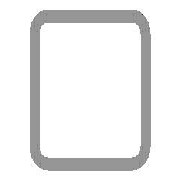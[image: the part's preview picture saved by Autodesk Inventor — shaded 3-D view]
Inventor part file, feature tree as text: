
AUTODESK INVENTOR PART (.ipt)
format: ipt  version: 2025.1 (Build 291241020, 241B)  size: 133,120 bytes
history: native  units: mm (DEFAULTED — no unit token found)
features: other x4, sketch x1, plane x1
ambient origin geometry x8: Origin, YZ Plane, XZ Plane, XY Plane, X Axis, Y Axis, Z Axis, Center Point
bodies: Solid1 (feature_tree), Body (feature_tree)
feature tree (6):
  parser-record x1  (decoder bookkeeping rows leaked as tree rows — omitted from the tree; the rows remain in map.json)
  other  "Driven Length"
  other  "Start Plane"
  other  "End Plane"
  sketch  "Sketch3"  dims[d3=1600.0mm d4=0.0mm d7=4.0mm d9=40.0mm d11=40.0mm d12=2.0mm d13=-0.0mm d14=1600.0mm d15=20.0mm d16=20.0mm d17=90.0deg d18=1600.0mm]
  plane  "Work Plane3"
